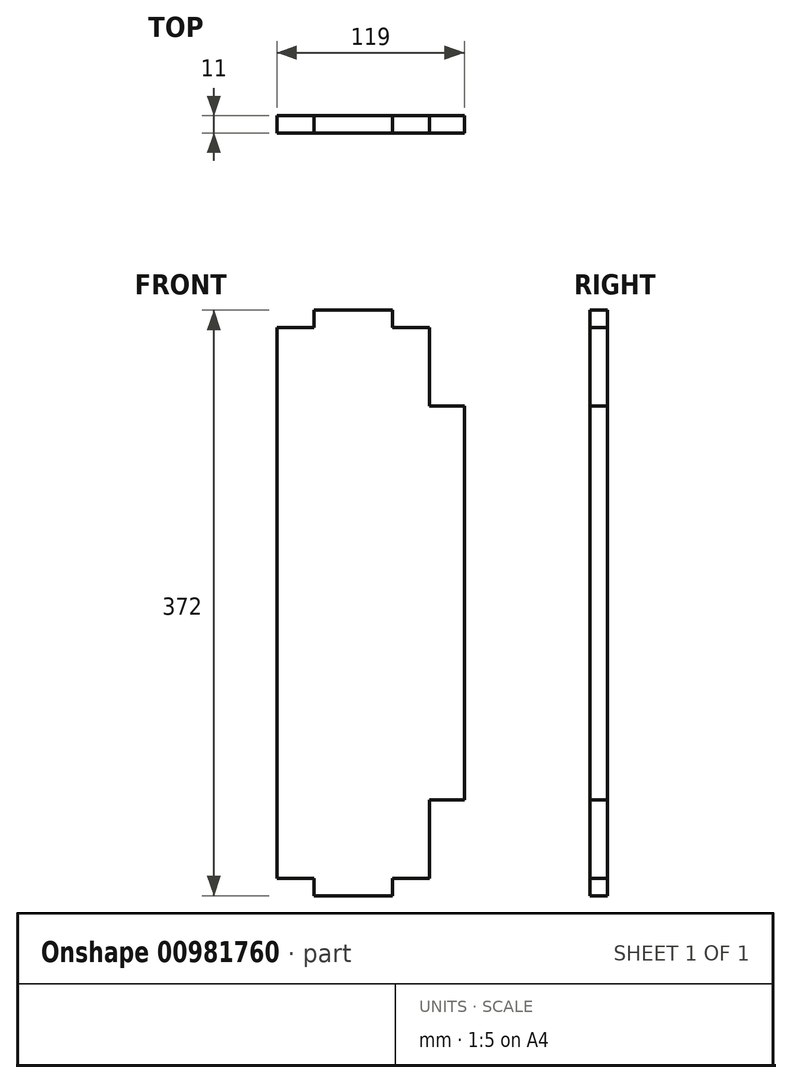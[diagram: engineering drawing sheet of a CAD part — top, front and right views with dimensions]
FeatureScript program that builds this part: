
annotation { "Feature Type Name" : "Feature", "Feature Type Description" : "" }
export const myFeature = defineFeature(function(context is Context, id is Id, definition is map)
    precondition{}
    {
        {
            var Q0;
            Q0=qCreatedBy(makeId("Front.planeOp"),FACE);
            var sketch = newSketch(context, id + "F0", { "sketchPlane" : qUnion([Q0])});
            skLineSegment(sketch, "E0", {"start": v(-59.5, -175) * mm, "end": v(-59.5, 175) * mm});
            skLineSegment(sketch, "E1", {"start": v(37.5, -175) * mm, "end": v(37.5, -125) * mm});
            skLineSegment(sketch, "E2", {"start": v(37.5, 125) * mm, "end": v(37.5, 175) * mm});
            skLineSegment(sketch, "E3", {"start": v(59.5, -125) * mm, "end": v(59.5, 125) * mm});
            skLineSegment(sketch, "E4", {"start": v(-59.5, 175) * mm, "end": v(-36, 175) * mm});
            skLineSegment(sketch, "E5", {"start": v(14, 175) * mm, "end": v(37.5, 175) * mm});
            skLineSegment(sketch, "E6", {"start": v(-36, 186) * mm, "end": v(14, 186) * mm});
            skLineSegment(sketch, "E7", {"start": v(-59.5, -175) * mm, "end": v(-36, -175) * mm});
            skLineSegment(sketch, "E8", {"start": v(14, -175) * mm, "end": v(37.5, -175) * mm});
            skLineSegment(sketch, "E9", {"start": v(37.5, -125) * mm, "end": v(59.5, -125) * mm});
            skLineSegment(sketch, "E10", {"start": v(37.5, 125) * mm, "end": v(59.5, 125) * mm});
            skLineSegment(sketch, "E11", {"start": v(-36, 186) * mm, "end": v(-36, 175) * mm});
            skLineSegment(sketch, "E12", {"start": v(14, 186) * mm, "end": v(14, 175) * mm});
            skLineSegment(sketch, "E13", {"start": v(-36, -186) * mm, "end": v(14, -186) * mm});
            skLineSegment(sketch, "E14", {"start": v(-36, -186) * mm, "end": v(-36, -175) * mm});
            skLineSegment(sketch, "E15", {"start": v(14, -186) * mm, "end": v(14, -175) * mm});
            skSolve(sketch);
        }
        {
            var Q0;
            Q0=makeQuery(id+"F0.imprint","IMPRINT",FACE,{"disambiguationData":[TD([[makeQuery(id+"F0.imprint","IMPRINT",EDGE,{"derivedFrom":sQuery(id+"F0.wireOp",EDGE,"E0")}),-1.0]])]});
            extrude(context, id + "F1", {"entities" : qUnion([Q0]), "depth" : 11 * mm, "offsetDistance" : 25 * mm});
        }
    });
